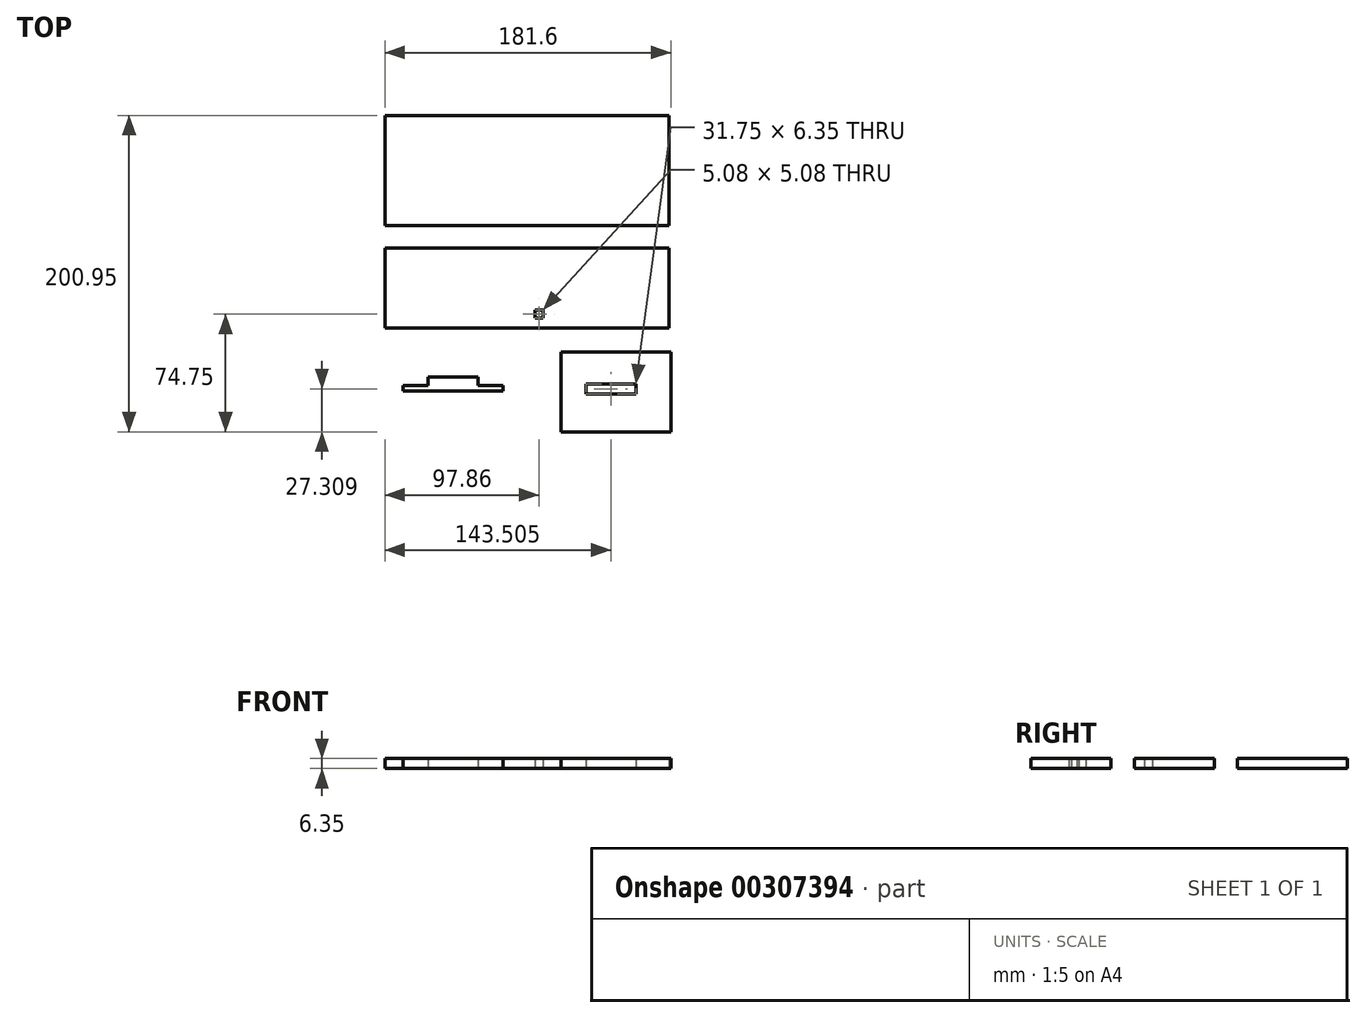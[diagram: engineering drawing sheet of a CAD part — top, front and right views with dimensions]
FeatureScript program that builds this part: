
annotation { "Feature Type Name" : "Feature", "Feature Type Description" : "" }
export const myFeature = defineFeature(function(context is Context, id is Id, definition is map)
    precondition{}
    {
        {
            var Q0;
            Q0=qCreatedBy(makeId("Top.planeOp"),FACE);
            var sketch = newSketch(context, id + "F0", { "sketchPlane" : qUnion([Q0])});
            skLineSegment(sketch, "E0.bottom", {"start": v(90.17, 25.4) * mm, "end": v(-90.17, 25.4) * mm});
            skLineSegment(sketch, "E0.top", {"start": v(90.17, -25.4) * mm, "end": v(-90.17, -25.4) * mm});
            skLineSegment(sketch, "E0.left", {"start": v(90.17, 25.4) * mm, "end": v(90.17, -25.4) * mm});
            skLineSegment(sketch, "E0.right", {"start": v(-90.17, 25.4) * mm, "end": v(-90.17, -25.4) * mm});
            skPoint(sketch, "E0.middle", {"position": v(0, 0) * mm});
            skLineSegment(sketch, "E1.bottom", {"start": v(10.16, -19.05) * mm, "end": v(5.08, -19.05) * mm});
            skLineSegment(sketch, "E1.top", {"start": v(10.16, -13.97) * mm, "end": v(5.08, -13.97) * mm});
            skLineSegment(sketch, "E1.left", {"start": v(10.16, -19.05) * mm, "end": v(10.16, -13.97) * mm});
            skLineSegment(sketch, "E1.right", {"start": v(5.08, -19.05) * mm, "end": v(5.08, -13.97) * mm});
            skPoint(sketch, "E1.middle", {"position": v(7.62, -16.51) * mm});
            skSolve(sketch);
        }
        {
            var Q0;
            Q0=makeQuery(id+"F0.imprint","IMPRINT",FACE,{"disambiguationData":[TD([[makeQuery(id+"F0.imprint","IMPRINT",EDGE,{"derivedFrom":sQuery(id+"F0.wireOp",EDGE,"E0.bottom")}),1.0]])]});
            extrude(context, id + "F1", {"entities" : qUnion([Q0]), "depth" : 6.35 * mm});
        }
        {
            var Q0;
            Q0=qCreatedBy(makeId("Top.planeOp"),FACE);
            var sketch = newSketch(context, id + "F2", { "sketchPlane" : qUnion([Q0])});
            skLineSegment(sketch, "E2.bottom", {"start": v(21.51, -40.46) * mm, "end": v(91.36, -40.46) * mm});
            skLineSegment(sketch, "E2.top", {"start": v(21.51, -91.26) * mm, "end": v(91.36, -91.26) * mm});
            skLineSegment(sketch, "E2.left", {"start": v(21.51, -40.46) * mm, "end": v(21.51, -91.26) * mm});
            skLineSegment(sketch, "E2.right", {"start": v(91.36, -40.46) * mm, "end": v(91.36, -91.26) * mm});
            skLineSegment(sketch, "E3.bottom", {"start": v(37.39, -60.78) * mm, "end": v(69.14, -60.78) * mm});
            skLineSegment(sketch, "E3.top", {"start": v(37.39, -67.13) * mm, "end": v(69.14, -67.13) * mm});
            skLineSegment(sketch, "E3.left", {"start": v(37.39, -60.78) * mm, "end": v(37.39, -67.13) * mm});
            skLineSegment(sketch, "E3.right", {"start": v(69.14, -60.78) * mm, "end": v(69.14, -67.13) * mm});
            skSolve(sketch);
        }
        {
            var Q0;
            Q0=makeQuery(id+"F2.imprint","IMPRINT",FACE,{"disambiguationData":[TD([[makeQuery(id+"F2.imprint","IMPRINT",EDGE,{"derivedFrom":sQuery(id+"F2.wireOp",EDGE,"E2.bottom")}),-1.0]])]});
            extrude(context, id + "F3", {"entities" : qUnion([Q0]), "depth" : 6.35 * mm});
        }
        {
            var Q0;
            Q0=qCreatedBy(makeId("Top.planeOp"),FACE);
            var sketch = newSketch(context, id + "F4", { "sketchPlane" : qUnion([Q0])});
            skLineSegment(sketch, "E4.bottom", {"start": v(-90.24, 39.84) * mm, "end": v(90.1, 39.84) * mm});
            skLineSegment(sketch, "E4.top", {"start": v(-90.24, 109.69) * mm, "end": v(90.1, 109.69) * mm});
            skLineSegment(sketch, "E4.left", {"start": v(-90.24, 39.84) * mm, "end": v(-90.24, 109.69) * mm});
            skLineSegment(sketch, "E4.right", {"start": v(90.1, 39.84) * mm, "end": v(90.1, 109.69) * mm});
            skSolve(sketch);
        }
        {
            var Q0;
            Q0=makeQuery(id+"F4.imprint","IMPRINT",FACE,{"disambiguationData":[TD([[makeQuery(id+"F4.imprint","IMPRINT",EDGE,{"derivedFrom":sQuery(id+"F4.wireOp",EDGE,"E4.bottom")}),1.0]])]});
            extrude(context, id + "F5", {"entities" : qUnion([Q0]), "depth" : 6.35 * mm});
        }
        {
            var Q0;
            Q0=qCreatedBy(makeId("Top.planeOp"),FACE);
            var sketch = newSketch(context, id + "F6", { "sketchPlane" : qUnion([Q0])});
            skLineSegment(sketch, "E5.bottom", {"start": v(-78.81, -61.88) * mm, "end": v(-62.94, -61.88) * mm});
            skLineSegment(sketch, "E5.top", {"start": v(-78.81, -65.43) * mm, "end": v(-15.31, -65.43) * mm});
            skLineSegment(sketch, "E5.left", {"start": v(-78.81, -61.88) * mm, "end": v(-78.81, -65.43) * mm});
            skLineSegment(sketch, "E5.right", {"start": v(-15.31, -61.88) * mm, "end": v(-15.31, -65.43) * mm});
            skLineSegment(sketch, "E6", {"start": v(-62.94, -61.88) * mm, "end": v(-62.94, -56.44) * mm});
            skLineSegment(sketch, "E7", {"start": v(-62.94, -56.44) * mm, "end": v(-31.19, -56.44) * mm});
            skLineSegment(sketch, "E8", {"start": v(-31.19, -56.44) * mm, "end": v(-31.19, -61.88) * mm});
            skLineSegment(sketch, "E9.trimOffspring", {"start": v(-31.19, -61.88) * mm, "end": v(-15.31, -61.88) * mm});
            skSolve(sketch);
        }
        {
            var Q0;
            Q0=makeQuery(id+"F6.imprint","IMPRINT",FACE,{"disambiguationData":[TD([[makeQuery(id+"F6.imprint","IMPRINT",EDGE,{"derivedFrom":sQuery(id+"F6.wireOp",EDGE,"E5.bottom")}),-1.0]])]});
            extrude(context, id + "F7", {"entities" : qUnion([Q0]), "depth" : 6.35 * mm});
        }
    });
